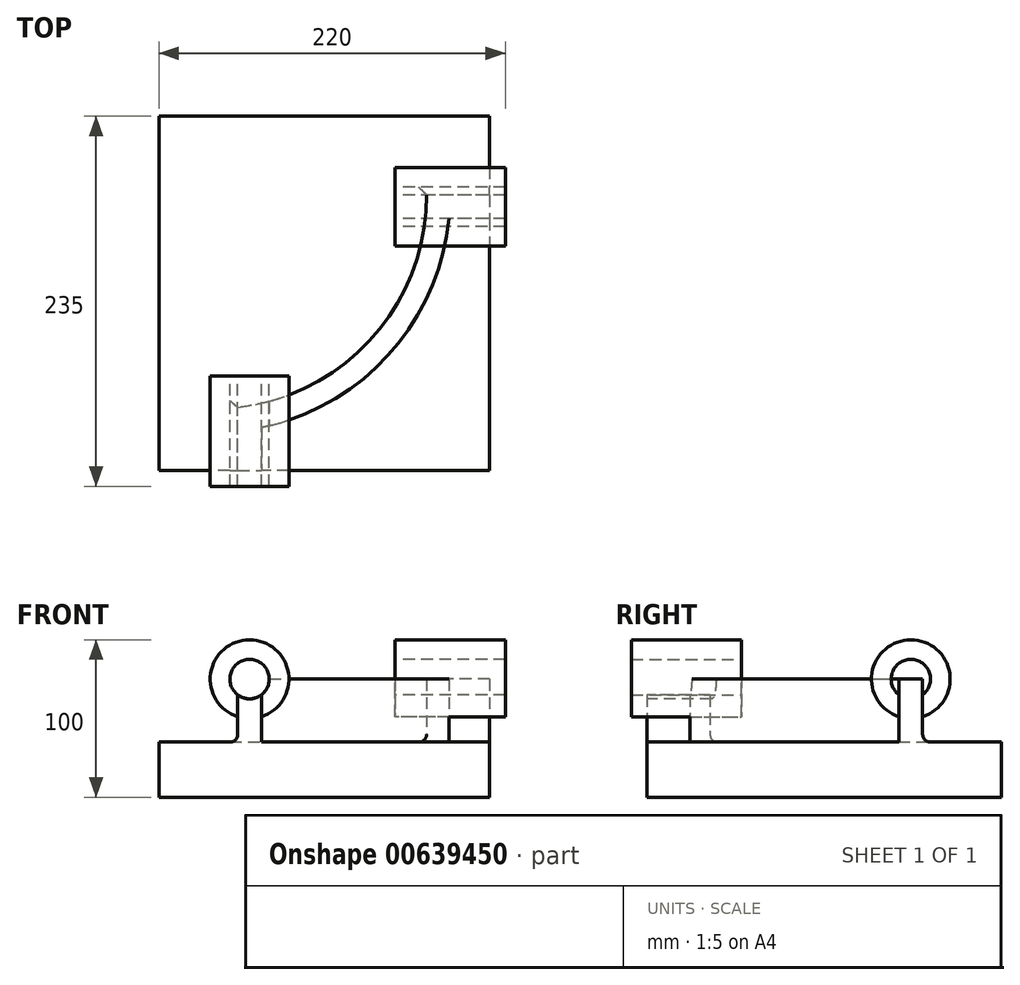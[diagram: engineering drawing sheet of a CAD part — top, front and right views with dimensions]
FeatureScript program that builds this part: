
annotation { "Feature Type Name" : "Feature", "Feature Type Description" : "" }
export const myFeature = defineFeature(function(context is Context, id is Id, definition is map)
    precondition{}
    {
        {
            var Q0;
            Q0=qCreatedBy(makeId("Top.planeOp"),FACE);
            var sketch = newSketch(context, id + "F0", { "sketchPlane" : qUnion([Q0])});
            skLineSegment(sketch, "E0.bottom", {"start": v(105, 112.5) * mm, "end": v(-105, 112.5) * mm});
            skLineSegment(sketch, "E0.top", {"start": v(105, -112.5) * mm, "end": v(-105, -112.5) * mm});
            skLineSegment(sketch, "E0.left", {"start": v(105, 112.5) * mm, "end": v(105, -112.5) * mm});
            skLineSegment(sketch, "E0.right", {"start": v(-105, 112.5) * mm, "end": v(-105, -112.5) * mm});
            skPoint(sketch, "E0.middle", {"position": v(0, 0) * mm});
            skLineSegment(sketch, "E1", {"start": v(105, 62.5) * mm, "end": v(65, 62.5) * mm});
            skLineSegment(sketch, "E2", {"start": v(-55, -112.5) * mm, "end": v(-55, -72.5) * mm});
            skArc(sketch, "E3", {"start": v(-55, -72.5) * mm, "mid": v(30.66, -27.81) * mm, "end": v(65, 62.5) * mm});
            skLineSegment(sketch, "E4", {"start": v(-70.94, 62.5) * mm, "end": v(65, 62.5) * mm, "construction": true});
            skLineSegment(sketch, "E5", {"start": v(-70.94, 62.5) * mm, "end": v(-55, -72.5) * mm, "construction": true});
            skLineSegment(sketch, "E6.0", {"start": v(105, 47.5) * mm, "end": v(79.25, 47.5) * mm});
            skArc(sketch, "E6.1", {"start": v(-40, -85.23) * mm, "mid": v(41.34, -38.38) * mm, "end": v(79.25, 47.5) * mm});
            skLineSegment(sketch, "E6.2", {"start": v(-40, -112.5) * mm, "end": v(-40, -85.23) * mm});
            skSolve(sketch);
        }
        {
            var Q0;
            {var subQ1=sQuery(id+"F0.wireOp",EDGE,"E1");Q0=makeQuery(id+"F0.imprint","IMPRINT",FACE,{"disambiguationData":[TD([[makeQuery(id+"F0.imprint","IMPRINT",EDGE,{"derivedFrom":subQ1}),1.0]])]});}
            extrude(context, id + "F1", {"entities" : qUnion([Q0]), "depth" : 40 * mm, "offsetDistance" : 25 * mm});
        }
        {
            var Q0;
            {var subQ2=sQuery(id+"F0.wireOp",EDGE,"E0.bottom");Q0=makeQuery(id+"F0.imprint","IMPRINT",FACE,{"disambiguationData":[TD([[makeQuery(id+"F0.imprint","IMPRINT",EDGE,{"derivedFrom":subQ2}),1.0]])]});}
            var Q1;
            {var subQ1=sQuery(id+"F0.wireOp",EDGE,"E1");Q1=makeQuery(id+"F0.imprint","IMPRINT",FACE,{"disambiguationData":[TD([[makeQuery(id+"F0.imprint","IMPRINT",EDGE,{"derivedFrom":subQ1}),1.0]])]});}
            var Q2;
            {var subQ4=sQuery(id+"F0.wireOp",EDGE,"E6.0");Q2=makeQuery(id+"F0.imprint","IMPRINT",FACE,{"disambiguationData":[TD([[makeQuery(id+"F0.imprint","IMPRINT",EDGE,{"derivedFrom":subQ4}),1.0]])]});}
            extrude(context, id + "F2", {"entities" : qUnion([Q0, Q1, Q2]), "operationType" : NewBodyOperationType.ADD, "oppositeDirection" : true, "depth" : 35 * mm, "offsetDistance" : 25 * mm});
        }
        {
            var Q0;
            {var subQ0=sQuery(id+"F0.wireOp",EDGE,"E0.top");Q0=makeQuery(id+"F2.boolean.opBoolean","MERGE",FACE,{"derivedFrom":[makeQuery(id+"F1.opExtrude","SWEPT_FACE",FACE,{"disambiguationData":[OSD([subQ0])]}),makeQuery(id+"F2.opExtrude","SWEPT_FACE",FACE,{"disambiguationData":[OSD([subQ0])]})]});}
            var sketch = newSketch(context, id + "F3", { "sketchPlane" : qUnion([Q0])});
            skCircle(sketch, "E7", {"center": v(-47.5, 40) * mm, "radius": 25 * mm});
            skCircle(sketch, "E8", {"center": v(-47.5, 40) * mm, "radius": 12.5 * mm});
            skSolve(sketch);
        }
        {
            var Q0;
            {var subQ0=sQuery(id+"F3.wireOp",EDGE,"E7");var subQ1=sQuery(id+"F0.wireOp",EDGE,"E0.top");var subQ2=makeQuery(id+"F1.opExtrude","SWEPT_EDGE",EDGE,{"disambiguationData":[OSD([subQ1,sQuery(id+"F0.wireOp",EDGE,"E2")])]});var subQ3=makeQuery(id+"F3.imprint","INTERSECT",VERTEX,{"derivedFrom":[subQ2,subQ0]});Q0=makeQuery(id+"F3.imprint","IMPRINT",FACE,{"disambiguationData":[TD([[makeQuery(id+"F3.imprint","IMPRINT",EDGE,{"disambiguationData":[TD([[subQ3,1.0]])],"derivedFrom":subQ0}),1.0]])]});}
            extrude(context, id + "F4", {"entities" : qUnion([Q0]), "depth" : 10 * mm, "offsetDistance" : 25 * mm, "hasSecondDirection" : true, "secondDirectionOppositeDirection" : true, "secondDirectionDepth" : 60 * mm});
        }
        {
            var Q0;
            {var subQ1=sQuery(id+"F0.wireOp",EDGE,"E0.top");var subQ6=makeQuery(id+"F1.opExtrude","CAP_EDGE",EDGE,{"disambiguationData":[OSD([subQ1])],"isStart":false});Q0=makeQuery(id+"F3.imprint","IMPRINT",FACE,{"disambiguationData":[TD([[makeQuery(id+"F3.imprint","IMPRINT",EDGE,{"derivedFrom":subQ6}),-1.0]])]});}
            var Q1;
            {var subQ1=sQuery(id+"F0.wireOp",EDGE,"E0.top");var subQ6=makeQuery(id+"F1.opExtrude","CAP_EDGE",EDGE,{"disambiguationData":[OSD([subQ1])],"isStart":false});Q1=makeQuery(id+"F3.imprint","IMPRINT",FACE,{"disambiguationData":[TD([[makeQuery(id+"F3.imprint","IMPRINT",EDGE,{"derivedFrom":subQ6}),1.0]])]});}
            extrude(context, id + "F5", {"entities" : qUnion([Q0, Q1]), "operationType" : NewBodyOperationType.REMOVE, "oppositeDirection" : true, "depth" : 50 * mm, "offsetDistance" : 25 * mm});
        }
        {
            var Q0;
            {var subQ0=sQuery(id+"F0.wireOp",EDGE,"E0.left");Q0=makeQuery(id+"F2.boolean.opBoolean","MERGE",FACE,{"derivedFrom":[makeQuery(id+"F1.opExtrude","SWEPT_FACE",FACE,{"disambiguationData":[OSD([subQ0])]}),makeQuery(id+"F2.opExtrude","SWEPT_FACE",FACE,{"disambiguationData":[OSD([subQ0])]})]});}
            var sketch = newSketch(context, id + "F6", { "sketchPlane" : qUnion([Q0])});
            skCircle(sketch, "E9", {"center": v(55, 40) * mm, "radius": 12.5 * mm});
            skCircle(sketch, "E10", {"center": v(55, 40) * mm, "radius": 25 * mm});
            skSolve(sketch);
        }
        {
            var Q0;
            {var subQ0=sQuery(id+"F6.wireOp",EDGE,"E9");var subQ1=sQuery(id+"F0.wireOp",EDGE,"E0.left");var subQ2=makeQuery(id+"F1.opExtrude","SWEPT_EDGE",EDGE,{"disambiguationData":[OSD([subQ1,sQuery(id+"F0.wireOp",EDGE,"E1")])]});var subQ3=makeQuery(id+"F6.imprint","INTERSECT",VERTEX,{"derivedFrom":[subQ2,subQ0]});Q0=makeQuery(id+"F6.imprint","IMPRINT",FACE,{"disambiguationData":[TD([[makeQuery(id+"F6.imprint","IMPRINT",EDGE,{"disambiguationData":[TD([[subQ3,-1.0]])],"derivedFrom":subQ0}),-1.0]])]});}
            extrude(context, id + "F7", {"entities" : qUnion([Q0]), "depth" : 10 * mm, "offsetDistance" : 25 * mm, "hasSecondDirection" : true, "secondDirectionOppositeDirection" : true, "secondDirectionDepth" : 60 * mm});
        }
        {
            var Q0;
            Q0=makeQuery(id+"F1.opExtrude","CAP_EDGE",EDGE,{"disambiguationData":[OSD([sQuery(id+"F0.wireOp",EDGE,"E6.1")])],"isStart":true});
            var Q1;
            Q1=makeQuery(id+"F1.opExtrude","CAP_EDGE",EDGE,{"disambiguationData":[OSD([sQuery(id+"F0.wireOp",EDGE,"E6.2")])],"isStart":true});
            var Q2;
            Q2=makeQuery(id+"F1.opExtrude","CAP_EDGE",EDGE,{"disambiguationData":[OSD([sQuery(id+"F0.wireOp",EDGE,"E6.0")])],"isStart":true});
            var Q3;
            Q3=makeQuery(id+"F1.opExtrude","CAP_EDGE",EDGE,{"disambiguationData":[OSD([sQuery(id+"F0.wireOp",EDGE,"E3")])],"isStart":true});
            var Q4;
            Q4=makeQuery(id+"F1.opExtrude","CAP_EDGE",EDGE,{"disambiguationData":[OSD([sQuery(id+"F0.wireOp",EDGE,"E1")])],"isStart":true});
            var Q5;
            Q5=makeQuery(id+"F1.opExtrude","CAP_EDGE",EDGE,{"disambiguationData":[OSD([sQuery(id+"F0.wireOp",EDGE,"E2")])],"isStart":true});
            fillet(context, id + "F8", {"entities" : qUnion([Q0, Q1, Q2, Q3, Q4, Q5]), "radius" : 5 * mm, "tangentPropagation" : true, "allowEdgeOverflow" : false});
        }
    });
